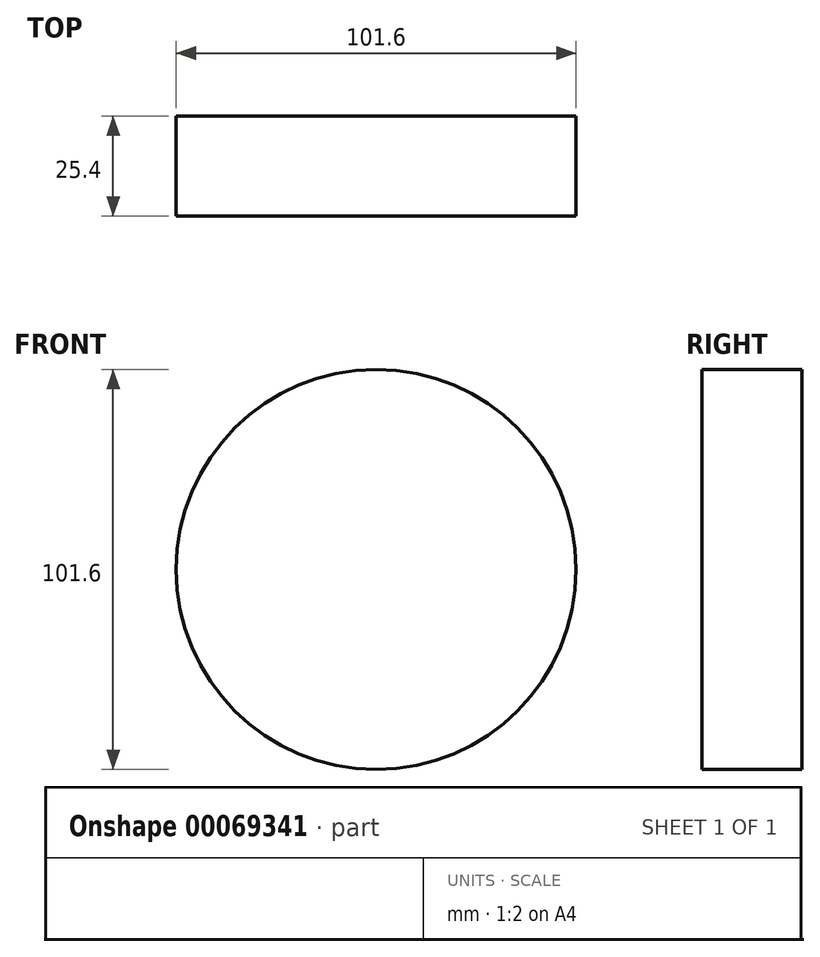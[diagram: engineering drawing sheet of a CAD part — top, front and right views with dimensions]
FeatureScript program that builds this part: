
annotation { "Feature Type Name" : "Feature", "Feature Type Description" : "" }
export const myFeature = defineFeature(function(context is Context, id is Id, definition is map)
    precondition{}
    {
        {
            var Q0;
            Q0=qCreatedBy(makeId("Front.planeOp"),FACE);
            var sketch = newSketch(context, id + "F0", { "sketchPlane" : qUnion([Q0])});
            skCircle(sketch, "E0", {"center": v(0, 0) * mm, "radius": 50.8 * mm});
            skSolve(sketch);
        }
        {
            var Q0;
            Q0=sQuery(id+"F0.wireOp",EDGE,"E0");
            extrude(context, id + "F1", {"bodyType" : ToolBodyType.SURFACE, "surfaceEntities" : qUnion([Q0]), "depth" : 25.4 * mm});
        }
    });
